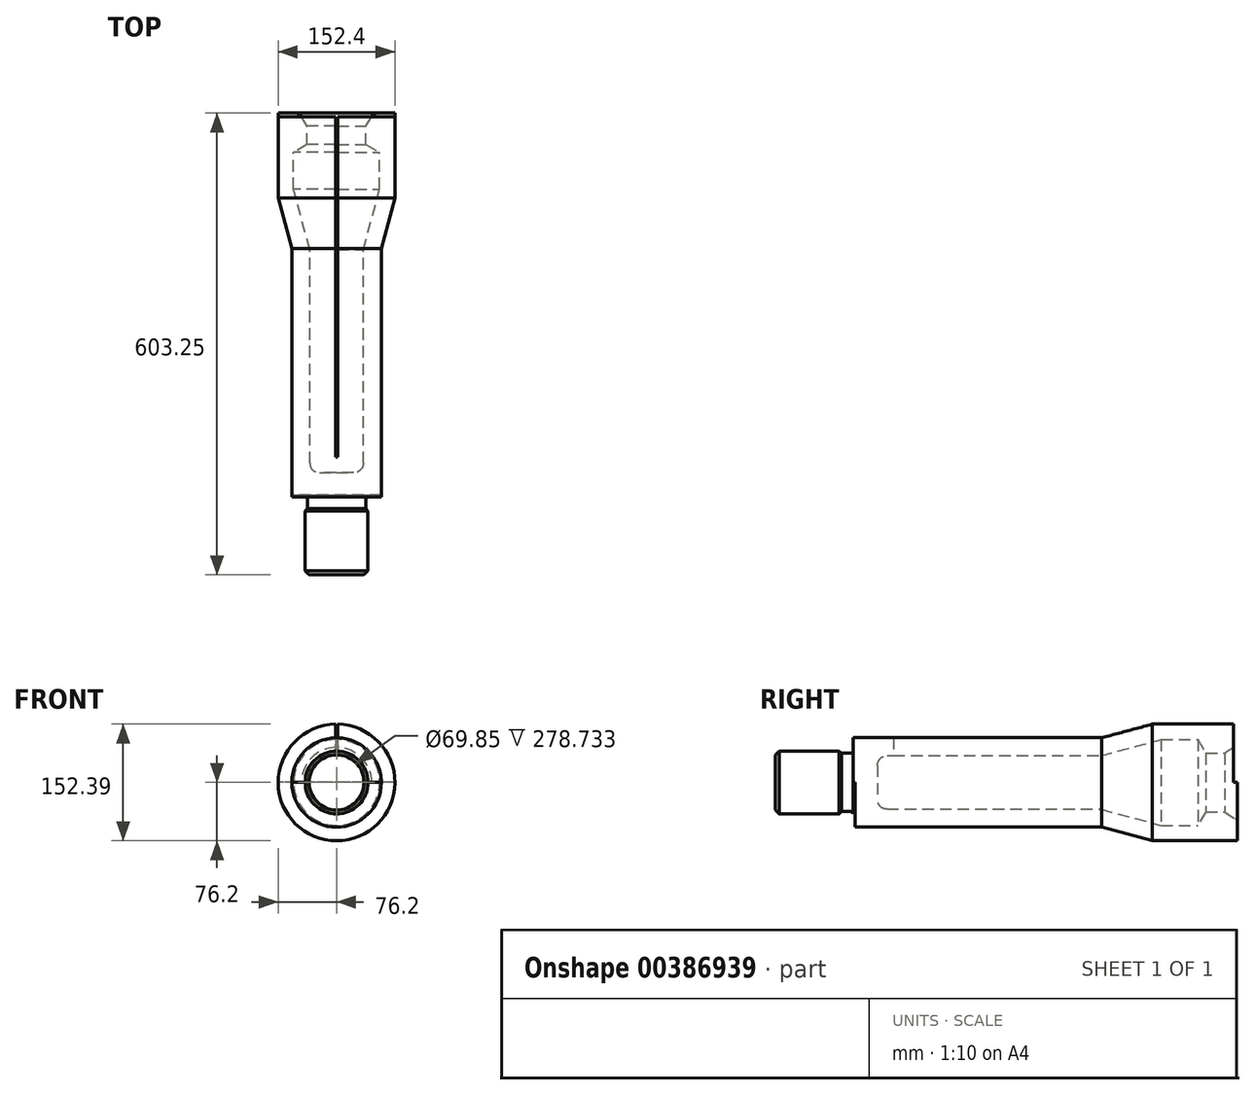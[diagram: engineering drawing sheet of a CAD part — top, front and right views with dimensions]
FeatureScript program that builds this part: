
annotation { "Feature Type Name" : "Feature", "Feature Type Description" : "" }
export const myFeature = defineFeature(function(context is Context, id is Id, definition is map)
    precondition{}
    {
        {
            var Q0;
            Q0=qCreatedBy(makeId("Front.planeOp"),FACE);
            var sketch = newSketch(context, id + "F0", { "sketchPlane" : qUnion([Q0])});
            skCircle(sketch, "E0", {"center": v(0, 0) * mm, "radius": 76.2 * mm});
            skSolve(sketch);
        }
        {
            var Q0;
            Q0 = qSketchRegion(id + "F0", true);
            extrude(context, id + "F1", {"entities" : qUnion([Q0]), "depth" : 501.65 * mm});
        }
        {
            var Q0;
            Q0=makeQuery(id+"F1.opExtrude","CAP_FACE",FACE,{"disambiguationData":[OSD([sQuery(id+"F0.wireOp",EDGE,"E0")])],"isStart":false});
            var sketch = newSketch(context, id + "F2", { "sketchPlane" : qUnion([Q0])});
            skCircle(sketch, "E1", {"center": v(0, 0) * mm, "radius": 41.05 * mm});
            skSolve(sketch);
        }
        {
            var Q0;
            Q0 = qSketchRegion(id + "F2", true);
            extrude(context, id + "F3", {"entities" : qUnion([Q0]), "operationType" : NewBodyOperationType.ADD, "depth" : 101.6 * mm});
        }
        {
            var Q0;
            Q0=qCreatedBy(makeId("Top.planeOp"),FACE);
            var sketch = newSketch(context, id + "F4", { "sketchPlane" : qUnion([Q0])});
            skLineSegment(sketch, "E2", {"start": v(47.04, -501.65) * mm, "end": v(41.15, -501.65) * mm});
            skLineSegment(sketch, "E3", {"start": v(0, -608.87) * mm, "end": v(0, -470.72) * mm});
            skLineSegment(sketch, "E4", {"start": v(38.1, -516.9) * mm, "end": v(38.1, -504.7) * mm});
            skLineSegment(sketch, "E5", {"start": v(38.1, -516.9) * mm, "end": v(46.16, -524.95) * mm});
            skLineSegment(sketch, "E6", {"start": v(46.16, -524.95) * mm, "end": v(47.04, -501.65) * mm});
            skPoint(sketch, "E7.orphan", {"position": v(0, -501.65) * mm});
            skPoint(sketch, "E8.visualSharp", {"position": v(38.1, -501.65) * mm});
            skArc(sketch, "E8.filletArc", {"start": v(41.15, -501.65) * mm, "mid": v(39, -502.54) * mm, "end": v(38.1, -504.7) * mm});
            skSolve(sketch);
        }
        {
            var Q0;
            Q0 = qSketchRegion(id + "F4", true);
            var Q1;
            Q1=sQuery(id+"F4.wireOp",EDGE,"E3");
            revolve(context, id + "F5", {"operationType" : NewBodyOperationType.REMOVE, "entities" : qUnion([Q0]), "axis" : qUnion([Q1]), "revolveType" : RevolveType.FULL, "oppositeDirection" : true});
        }
        {
            var Q0;
            Q0=makeQuery(id+"F3.opExtrude","CAP_EDGE",EDGE,{"disambiguationData":[OSD([sQuery(id+"F2.wireOp",EDGE,"E1")])],"isStart":false});
            chamfer(context, id + "F6", {"entities" : qUnion([Q0]), "width" : 5.08 * mm, "tangentPropagation" : true});
        }
        {
            var Q0;
            Q0=qCreatedBy(makeId("Top.planeOp"),FACE);
            var sketch = newSketch(context, id + "F7", { "sketchPlane" : qUnion([Q0])});
            skLineSegment(sketch, "E9", {"start": v(0, 0) * mm, "end": v(0, -469.9) * mm});
            skLineSegment(sketch, "E10", {"start": v(47.15, -2.94) * mm, "end": v(38.35, -16.75) * mm});
            skLineSegment(sketch, "E11", {"start": v(38.35, -16.75) * mm, "end": v(38.35, -41.15) * mm});
            skLineSegment(sketch, "E12", {"start": v(38.35, -41.15) * mm, "end": v(56.13, -51.41) * mm});
            skLineSegment(sketch, "E13", {"start": v(56.13, -51.41) * mm, "end": v(56.13, -99.31) * mm});
            skLineSegment(sketch, "E14", {"start": v(56.13, -99.31) * mm, "end": v(34.92, -178.47) * mm});
            skLineSegment(sketch, "E15", {"start": v(34.92, -178.47) * mm, "end": v(34.93, -457.2) * mm});
            skLineSegment(sketch, "E16", {"start": v(22.23, -469.9) * mm, "end": v(0, -469.9) * mm});
            skArc(sketch, "E17.filletArc", {"start": v(22.23, -469.9) * mm, "mid": v(31.2, -466.18) * mm, "end": v(34.93, -457.2) * mm});
            skPoint(sketch, "E18.visualSharp", {"position": v(49.02, 0) * mm});
            skArc(sketch, "E18.filletArc", {"start": v(52.5, 0) * mm, "mid": v(49.45, -0.78) * mm, "end": v(47.15, -2.94) * mm});
            skLineSegment(sketch, "E19", {"start": v(52.5, 0) * mm, "end": v(57.8, 10.05) * mm});
            skLineSegment(sketch, "E20", {"start": v(57.8, 10.05) * mm, "end": v(24.83, 11.3) * mm});
            skLineSegment(sketch, "E21", {"start": v(24.83, 11.3) * mm, "end": v(0, 0) * mm});
            skSolve(sketch);
        }
        {
            var Q0;
            Q0=qCreatedBy(makeId("Top.planeOp"),FACE);
            var sketch = newSketch(context, id + "F8", { "sketchPlane" : qUnion([Q0])});
            skLineSegment(sketch, "E22", {"start": v(76.2, -110.74) * mm, "end": v(76.2, 3.66) * mm});
            skPoint(sketch, "E23", {"position": v(76.2, -110.74) * mm});
            skLineSegment(sketch, "E24", {"start": v(76.2, -110.74) * mm, "end": v(58.42, -177.1) * mm});
            skLineSegment(sketch, "E25", {"start": v(58.42, -484.96) * mm, "end": v(58.42, -177.1) * mm});
            skLineSegment(sketch, "E26", {"start": v(58.42, -484.96) * mm, "end": v(58.42, -521.4) * mm});
            skLineSegment(sketch, "E27", {"start": v(58.42, -521.4) * mm, "end": v(105.83, -521.4) * mm});
            skLineSegment(sketch, "E28", {"start": v(105.83, -521.4) * mm, "end": v(122.15, -191.54) * mm});
            skLineSegment(sketch, "E29", {"start": v(122.15, -191.54) * mm, "end": v(76.2, -110.74) * mm});
            skSolve(sketch);
        }
        {
            var Q0;
            Q0 = qSketchRegion(id + "F7", true);
            var Q1;
            Q1=makeQuery(id+"F1.opExtrude","SWEPT_FACE",FACE,{"disambiguationData":[OSD([sQuery(id+"F0.wireOp",EDGE,"E0")])]});
            revolve(context, id + "F9", {"operationType" : NewBodyOperationType.REMOVE, "entities" : qUnion([Q0]), "axis" : qUnion([Q1]), "revolveType" : RevolveType.FULL, "oppositeDirection" : true});
        }
        {
            var Q0;
            Q0 = qSketchRegion(id + "F8", true);
            var Q1;
            Q1=makeQuery(id+"F1.opExtrude","SWEPT_FACE",FACE,{"disambiguationData":[OSD([sQuery(id+"F0.wireOp",EDGE,"E0")])]});
            revolve(context, id + "F10", {"operationType" : NewBodyOperationType.REMOVE, "entities" : qUnion([Q0]), "axis" : qUnion([Q1]), "revolveType" : RevolveType.FULL, "oppositeDirection" : true});
        }
        {
            var Q0;
            Q0=qCreatedBy(makeId("Top.planeOp"),FACE);
            var sketch = newSketch(context, id + "F11", { "sketchPlane" : qUnion([Q0])});
            skLineSegment(sketch, "E30", {"start": v(0, 0) * mm, "end": v(0, -449.07) * mm});
            skLineSegment(sketch, "E31.0", {"start": v(1.17, 0) * mm, "end": v(1.17, -449.07) * mm});
            skLineSegment(sketch, "E32.MirrorCS", {"start": v(-1.17, 0) * mm, "end": v(-1.17, -449.07) * mm});
            skLineSegment(sketch, "E33", {"start": v(1.17, -449.07) * mm, "end": v(-1.17, -449.07) * mm});
            skLineSegment(sketch, "E34", {"start": v(1.17, 0) * mm, "end": v(-1.17, 0) * mm});
            skSolve(sketch);
        }
        {
            var Q0;
            Q0 = qSketchRegion(id + "F11", true);
            extrude(context, id + "F12", {"entities" : qUnion([Q0]), "operationType" : NewBodyOperationType.REMOVE, "depth" : 104.4 * mm});
        }
        {
            var Q0;
            Q0=qCreatedBy(makeId("Front.planeOp"),FACE);
            cPlane(context, id + "F13", {"entities" : qUnion([Q0]), "cplaneType" : CPlaneType.OFFSET, "offset" : 501.65 * mm, "width" : 152.4 * mm, "height" : 152.4 * mm});
        }
        {
            var Q0;
            Q0=qCreatedBy(id+"F13.planeOp",FACE);
            var sketch = newSketch(context, id + "F14", { "sketchPlane" : qUnion([Q0])});
            skLineSegment(sketch, "E35", {"start": v(84.7, 0) * mm, "end": v(-85.19, 0) * mm});
            skLineSegment(sketch, "E36", {"start": v(-85.19, 0) * mm, "end": v(-16.16, -94.98) * mm});
            skLineSegment(sketch, "E37", {"start": v(-16.16, -94.98) * mm, "end": v(63.64, -83.23) * mm});
            skLineSegment(sketch, "E38", {"start": v(63.64, -83.23) * mm, "end": v(99.87, -39.66) * mm});
            skLineSegment(sketch, "E39", {"start": v(99.87, -39.66) * mm, "end": v(84.7, 0) * mm});
            skSolve(sketch);
        }
        {
            var Q0;
            Q0 = qSketchRegion(id + "F14", true);
            extrude(context, id + "F15", {"entities" : qUnion([Q0]), "operationType" : NewBodyOperationType.REMOVE, "oppositeDirection" : true, "depth" : 2.54 * mm});
        }
        {
            var Q0;
            Q0=qCreatedBy(makeId("Front.planeOp"),FACE);
            var sketch = newSketch(context, id + "F16", { "sketchPlane" : qUnion([Q0])});
            skLineSegment(sketch, "E40.bottom", {"start": v(0, 0) * mm, "end": v(-94.75, 0) * mm});
            skLineSegment(sketch, "E40.top", {"start": v(0, 80.58) * mm, "end": v(-94.75, 80.58) * mm});
            skLineSegment(sketch, "E40.right", {"start": v(-94.75, 0) * mm, "end": v(-94.75, 80.58) * mm});
            skLineSegment(sketch, "E41.MirrorCS", {"start": v(0, 80.58) * mm, "end": v(94.75, 80.58) * mm});
            skLineSegment(sketch, "E42.MirrorCS", {"start": v(94.75, 0) * mm, "end": v(94.75, 80.58) * mm});
            skLineSegment(sketch, "E43.MirrorCS", {"start": v(0, 0) * mm, "end": v(94.75, 0) * mm});
            skSolve(sketch);
        }
        {
            var Q0;
            Q0 = qSketchRegion(id + "F16", true);
            extrude(context, id + "F17", {"entities" : qUnion([Q0]), "operationType" : NewBodyOperationType.REMOVE, "depth" : 5 * mm, "offsetDistance" : 25 * mm});
        }
    });
